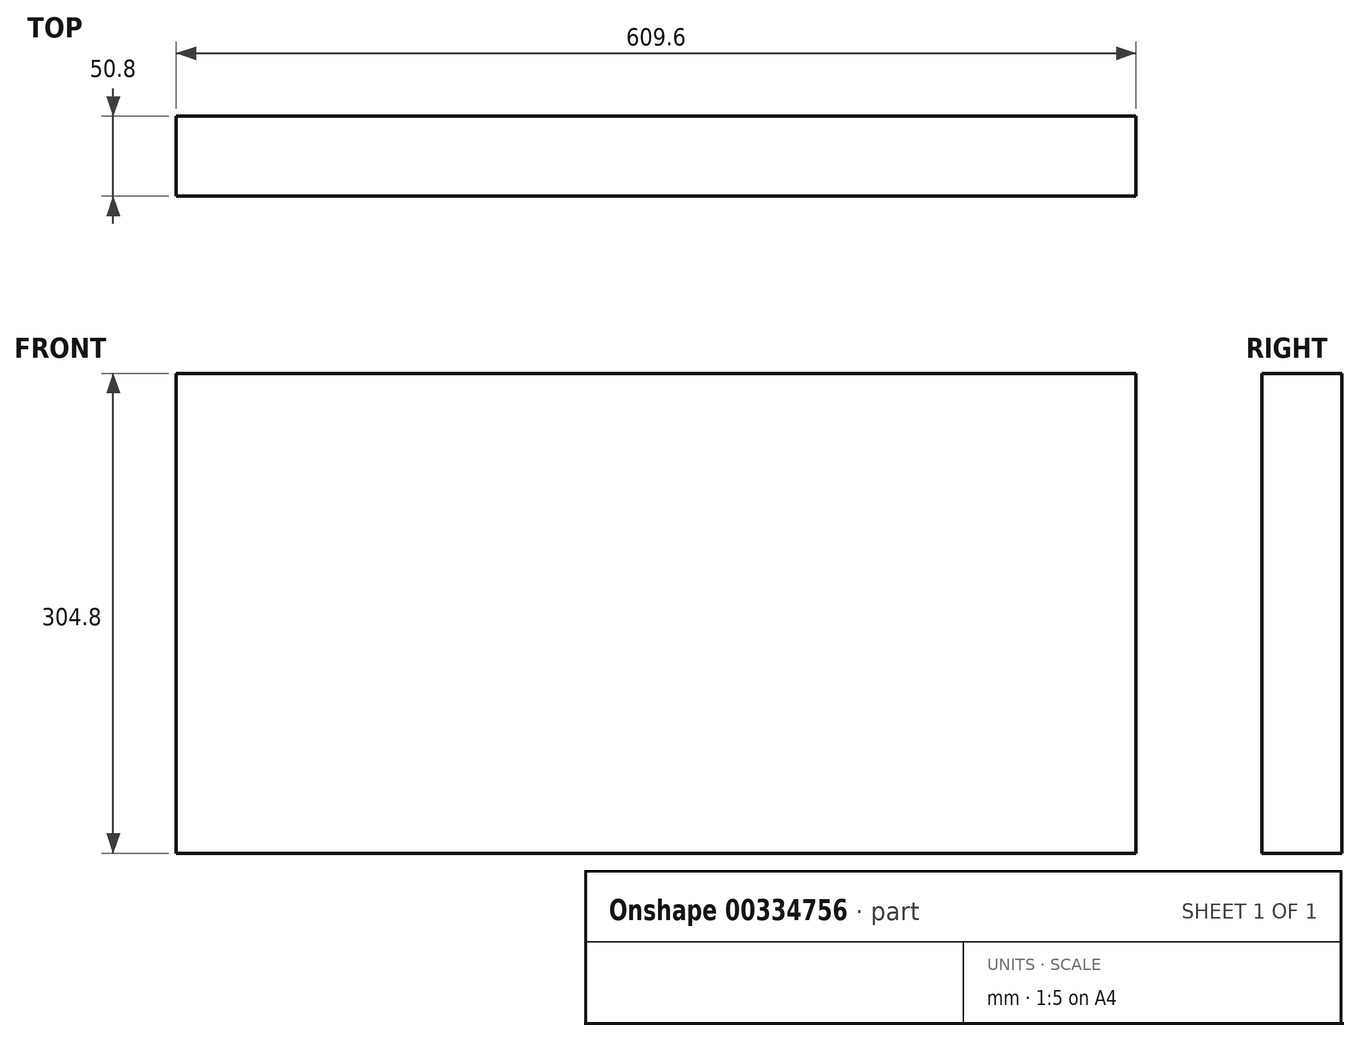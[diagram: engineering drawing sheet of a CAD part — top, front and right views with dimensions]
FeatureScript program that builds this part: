
annotation { "Feature Type Name" : "Feature", "Feature Type Description" : "" }
export const myFeature = defineFeature(function(context is Context, id is Id, definition is map)
    precondition{}
    {
        {
            var Q0;
            Q0=qCreatedBy(makeId("Front.planeOp"),FACE);
            var sketch = newSketch(context, id + "F0", { "sketchPlane" : qUnion([Q0])});
            skLineSegment(sketch, "E0.bottom", {"start": v(0, 0) * mm, "end": v(609.6, 0) * mm});
            skLineSegment(sketch, "E0.top", {"start": v(0, 304.8) * mm, "end": v(609.6, 304.8) * mm});
            skLineSegment(sketch, "E0.left", {"start": v(0, 0) * mm, "end": v(0, 304.8) * mm});
            skLineSegment(sketch, "E0.right", {"start": v(609.6, 0) * mm, "end": v(609.6, 304.8) * mm});
            skSolve(sketch);
        }
        {
            var Q0;
            Q0 = qSketchRegion(id + "F0", true);
            extrude(context, id + "F1", {"entities" : qUnion([Q0]), "depth" : 50.8 * mm});
        }
    });
